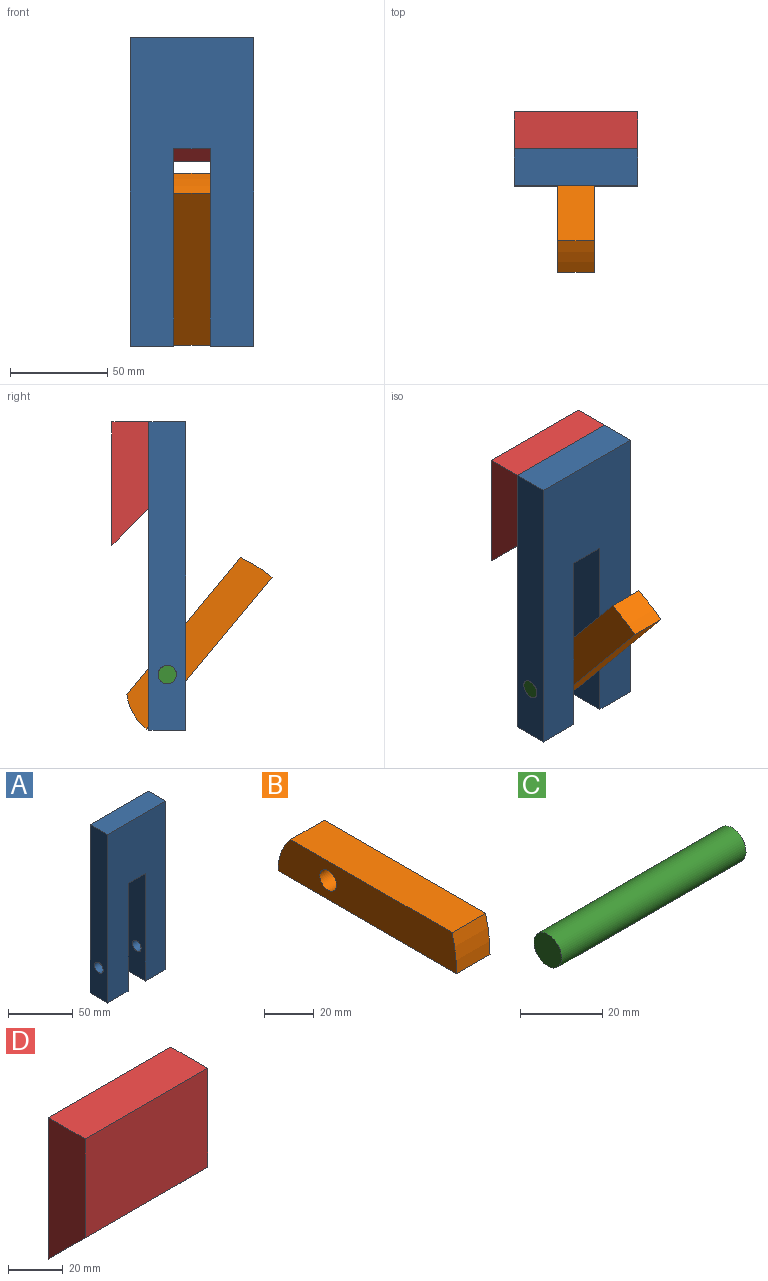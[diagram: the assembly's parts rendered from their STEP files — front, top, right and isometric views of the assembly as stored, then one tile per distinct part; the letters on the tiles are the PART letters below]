
ASSEMBLY  parts=4 mates=5
PART A: 12 faces, bbox 63.5x19.1x158.8 mm
  f0: plane 22.23x19.05mm, normal (0,0,-1), area 423.4mm2, adj f1,f2,f4,f7
  f1: plane 158.75x19.05mm, normal (1,0,0), area 2952.9mm2, adj f0,f2,f4,f6,f11
  f2: plane 158.75x63.5mm, normal (0,1,0), area 8145.1mm2, adj f0,f1,f3,f5,f6,f7,f8,f9
  f3: plane 158.75x19.05mm, normal (-1,0,0), area 2952.9mm2, adj f2,f4,f5,f6,f10
  f4: plane 158.75x63.5mm, normal (0,-1,0), area 8145.1mm2, adj f0,f1,f3,f5,f6,f7,f8,f9
  f5: plane 22.23x19.05mm, normal (0,0,-1), area 423.4mm2, adj f2,f3,f4,f9
  f6: plane 63.5x19.05mm, normal (0,0,1), area 1209.7mm2, adj f1,f2,f3,f4
  f7: plane 101.6x19.05mm, normal (-1,0,0), area 1864.2mm2, adj f0,f2,f4,f8,f11
  f8: plane 19.05x19.05mm, normal (0,0,-1), area 362.9mm2, adj f2,f4,f7,f9
  f9: plane 101.6x19.05mm, normal (1,0,0), area 1864.2mm2, adj f2,f4,f5,f8,f10
  f10: cylinder r=4.76mm len=22.23mm, axis (-1,0,0), area 665.1mm2, adj f3,f9
  f11: cylinder r=4.76mm len=22.23mm, axis (-1,0,0), area 665.1mm2, adj f1,f7
PART B: 7 faces, bbox 19.1x101.6x19.1 mm
  f0: plane 91.8x19.05mm, normal (0,0,1), area 1748.7mm2, adj f1,f3,f4,f5
  f1: cylinder r=28.57mm len=19.05mm, axis (1,0,0), area 397.2mm2, adj f0,f2,f4,f5
  f2: plane 101.6x19.05mm, normal (0,0,-1), area 1935.5mm2, adj f1,f3,f4,f5
  f3: cylinder r=73.03mm len=19.05mm, axis (1,0,0), area 367.1mm2, adj f0,f2,f4,f5
  f4: plane 101.6x19.05mm, normal (-1,0,0), area 1804.7mm2, adj f0,f1,f2,f3,f6
  f5: plane 101.6x19.05mm, normal (1,0,0), area 1804.7mm2, adj f0,f1,f2,f3,f6
  f6: cylinder r=4.76mm len=19.05mm, axis (-1,0,0), area 570mm2, adj f4,f5
PART C: 3 faces, bbox 63.5x9.5x9.5 mm
  f0: plane 9.53x9.53mm, normal (1,0,0), area 71.3mm2, adj f1
  f1: cylinder r=4.76mm len=63.5mm, axis (-1,0,0), area 1900.2mm2, adj f0,f2
  f2: plane 9.53x9.53mm, normal (-1,0,0), area 71.3mm2, adj f1
PART D: 6 faces, bbox 63.5x19.1x63.5 mm
  f0: plane 63.5x44.45mm, normal (0,-1,0), area 2822.6mm2, adj f1,f3,f4,f5
  f1: plane 63.5x19.05mm, normal (0,-0.71,-0.71), area 1710.7mm2, adj f0,f2,f4,f5
  f2: plane 63.5x63.5mm, normal (0,1,0), area 4032.3mm2, adj f1,f3,f4,f5
  f3: plane 63.5x19.05mm, normal (0,0,1), area 1209.7mm2, adj f0,f2,f4,f5
  f4: plane 63.5x19.05mm, normal (1,0,0), area 1028.2mm2, adj f0,f1,f2,f3
  f5: plane 63.5x19.05mm, normal (-1,0,0), area 1028.2mm2, adj f0,f1,f2,f3
PLACE A t=(0,0,-120.65)mm
PLACE B rot(axis=(-1,0,0),50.3deg) t=(0,-3,-146.09)mm
PLACE C t=(0,0,-120.65)mm
PLACE D t=(0,0,-120.65)mm
MATE fastened D.f5 <-> A.f3  axis (-1,0,0) through (0,-19.05,0)mm
MATE planar C.f1 <-> A.f10  axis (-1,0,0) through (0,-28.57,-130.17)mm
MATE planar B.f4 <-> A.f9  axis (-1,0,0) through (22.23,-43.91,-111.93)mm
MATE cylindrical C.f1 <-> B.f6  axis (-1,0,0) through (31.75,-28.57,-130.17)mm
MATE cylindrical A.f10 <-> C.f1  axis (-1,0,0) through (0,-28.57,-130.17)mm
